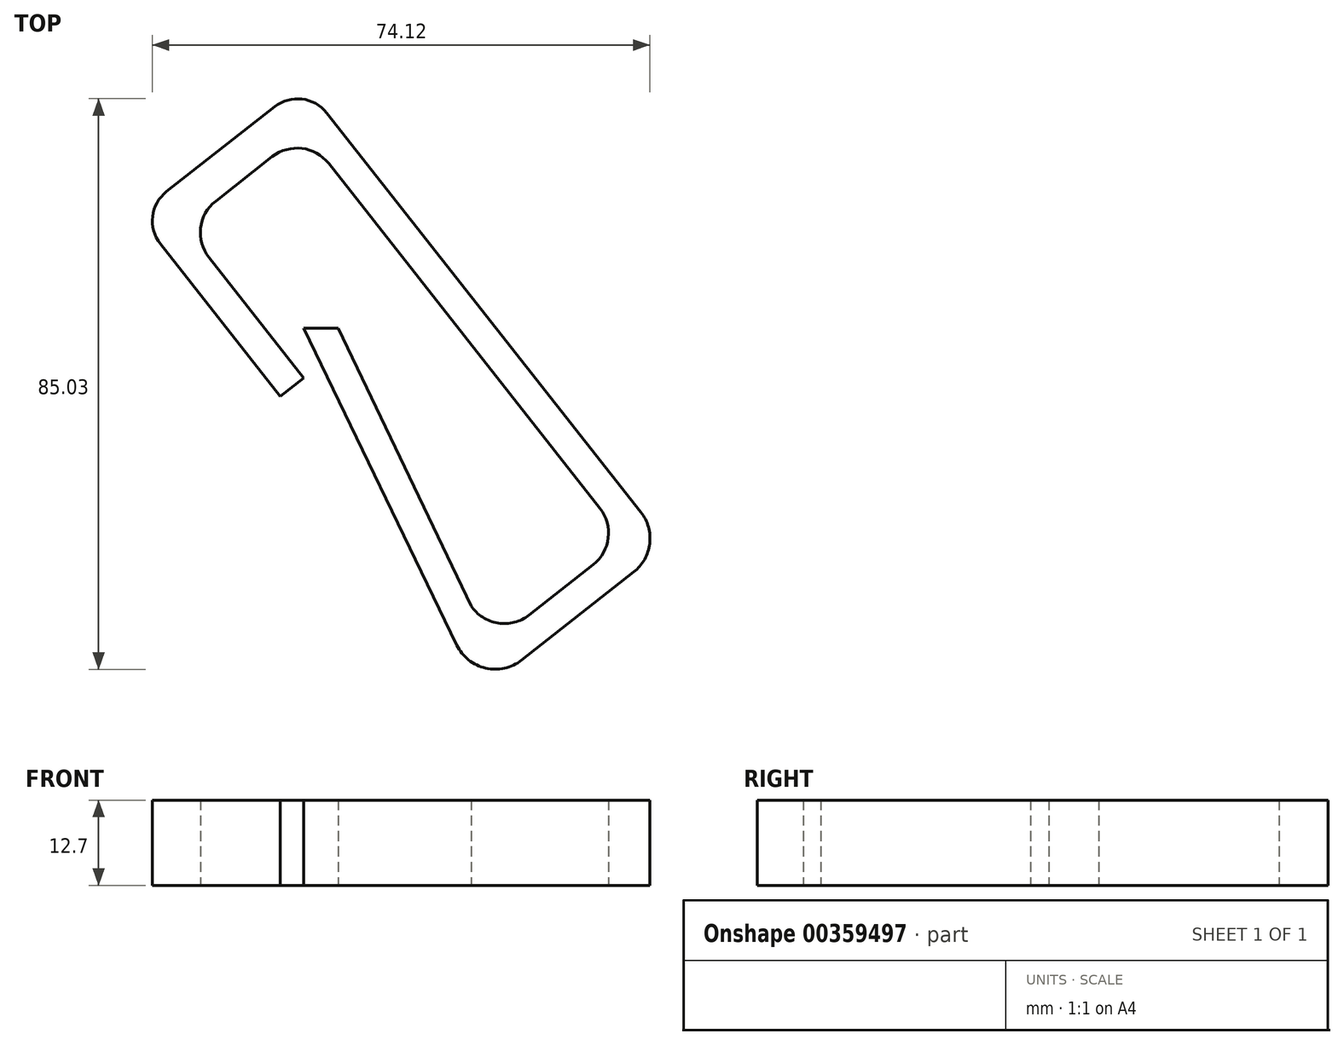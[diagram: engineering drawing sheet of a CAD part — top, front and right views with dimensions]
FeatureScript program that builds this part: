
annotation { "Feature Type Name" : "Feature", "Feature Type Description" : "" }
export const myFeature = defineFeature(function(context is Context, id is Id, definition is map)
    precondition{}
    {
        {
            var Q0;
            Q0=qCreatedBy(makeId("Top.planeOp"),FACE);
            var sketch = newSketch(context, id + "F0", { "sketchPlane" : qUnion([Q0])});
            skLineSegment(sketch, "E0", {"start": v(0, 0) * mm, "end": v(-14.13, 17.98) * mm});
            skLineSegment(sketch, "E1", {"start": v(-13.13, 26.37) * mm, "end": v(-4.7, 33) * mm});
            skLineSegment(sketch, "E2", {"start": v(3.7, 32) * mm, "end": v(44.11, -19.42) * mm});
            skLineSegment(sketch, "E3", {"start": v(47.8, -24.12) * mm, "end": v(47.8, -24.12) * mm});
            skPoint(sketch, "E4.end.orphan", {"position": v(0, 7.44) * mm});
            skPoint(sketch, "E5.visualSharp", {"position": v(-17.83, 22.68) * mm});
            skArc(sketch, "E5.filletArc", {"start": v(-13.13, 26.37) * mm, "mid": v(-15.37, 22.38) * mm, "end": v(-14.13, 17.98) * mm});
            skPoint(sketch, "E6.visualSharp", {"position": v(0, 36.69) * mm});
            skArc(sketch, "E6.filletArc", {"start": v(3.7, 32) * mm, "mid": v(-0.3, 34.23) * mm, "end": v(-4.7, 33) * mm});
            skLineSegment(sketch, "E7", {"start": v(43.1, -27.8) * mm, "end": v(33.56, -35.31) * mm});
            skPoint(sketch, "E8.visualSharp", {"position": v(23.9, -42.9) * mm});
            skArc(sketch, "E8.filletArc", {"start": v(24.9, -33.94) * mm, "mid": v(28.93, -36.52) * mm, "end": v(33.56, -35.31) * mm});
            skArc(sketch, "E9.filletArc", {"start": v(43.1, -27.8) * mm, "mid": v(45.35, -23.82) * mm, "end": v(44.11, -19.42) * mm});
            skLineSegment(sketch, "E10", {"start": v(0, 0) * mm, "end": v(-3.49, -2.74) * mm});
            skLineSegment(sketch, "E11", {"start": v(-3.49, -2.74) * mm, "end": v(-21.38, 20) * mm});
            skLineSegment(sketch, "E12", {"start": v(-20.44, 27.8) * mm, "end": v(-4.36, 40.44) * mm});
            skPoint(sketch, "E13.visualSharp", {"position": v(-24.8, 24.37) * mm});
            skArc(sketch, "E13.filletArc", {"start": v(-20.44, 27.8) * mm, "mid": v(-22.52, 24.1) * mm, "end": v(-21.38, 20) * mm});
            skLineSegment(sketch, "E14", {"start": v(3.43, 39.5) * mm, "end": v(50.2, -20) * mm});
            skPoint(sketch, "E15.visualSharp", {"position": v(0, 43.87) * mm});
            skArc(sketch, "E15.filletArc", {"start": v(3.43, 39.5) * mm, "mid": v(-0.27, 41.59) * mm, "end": v(-4.36, 40.44) * mm});
            skLineSegment(sketch, "E16", {"start": v(49.14, -28.9) * mm, "end": v(32.43, -42.04) * mm});
            skPoint(sketch, "E17.visualSharp", {"position": v(54.13, -24.98) * mm});
            skArc(sketch, "E17.filletArc", {"start": v(49.14, -28.9) * mm, "mid": v(51.52, -24.67) * mm, "end": v(50.2, -20) * mm});
            skLineSegment(sketch, "E18", {"start": v(22.8, -39.81) * mm, "end": v(0, 7.44) * mm});
            skLineSegment(sketch, "E19", {"start": v(24.9, -33.94) * mm, "end": v(5.1, 7.44) * mm});
            skPoint(sketch, "E20.visualSharp", {"position": v(26.23, -46.92) * mm});
            skArc(sketch, "E20.filletArc", {"start": v(22.8, -39.81) * mm, "mid": v(27.08, -43.23) * mm, "end": v(32.43, -42.04) * mm});
            skLineSegment(sketch, "E21", {"start": v(5.1, 7.44) * mm, "end": v(0, 7.44) * mm});
            skSolve(sketch);
        }
        {
            var Q0;
            Q0 = qSketchRegion(id + "F0", true);
            extrude(context, id + "F1", {"entities" : qUnion([Q0]), "depth" : 12.7 * mm});
        }
    });
